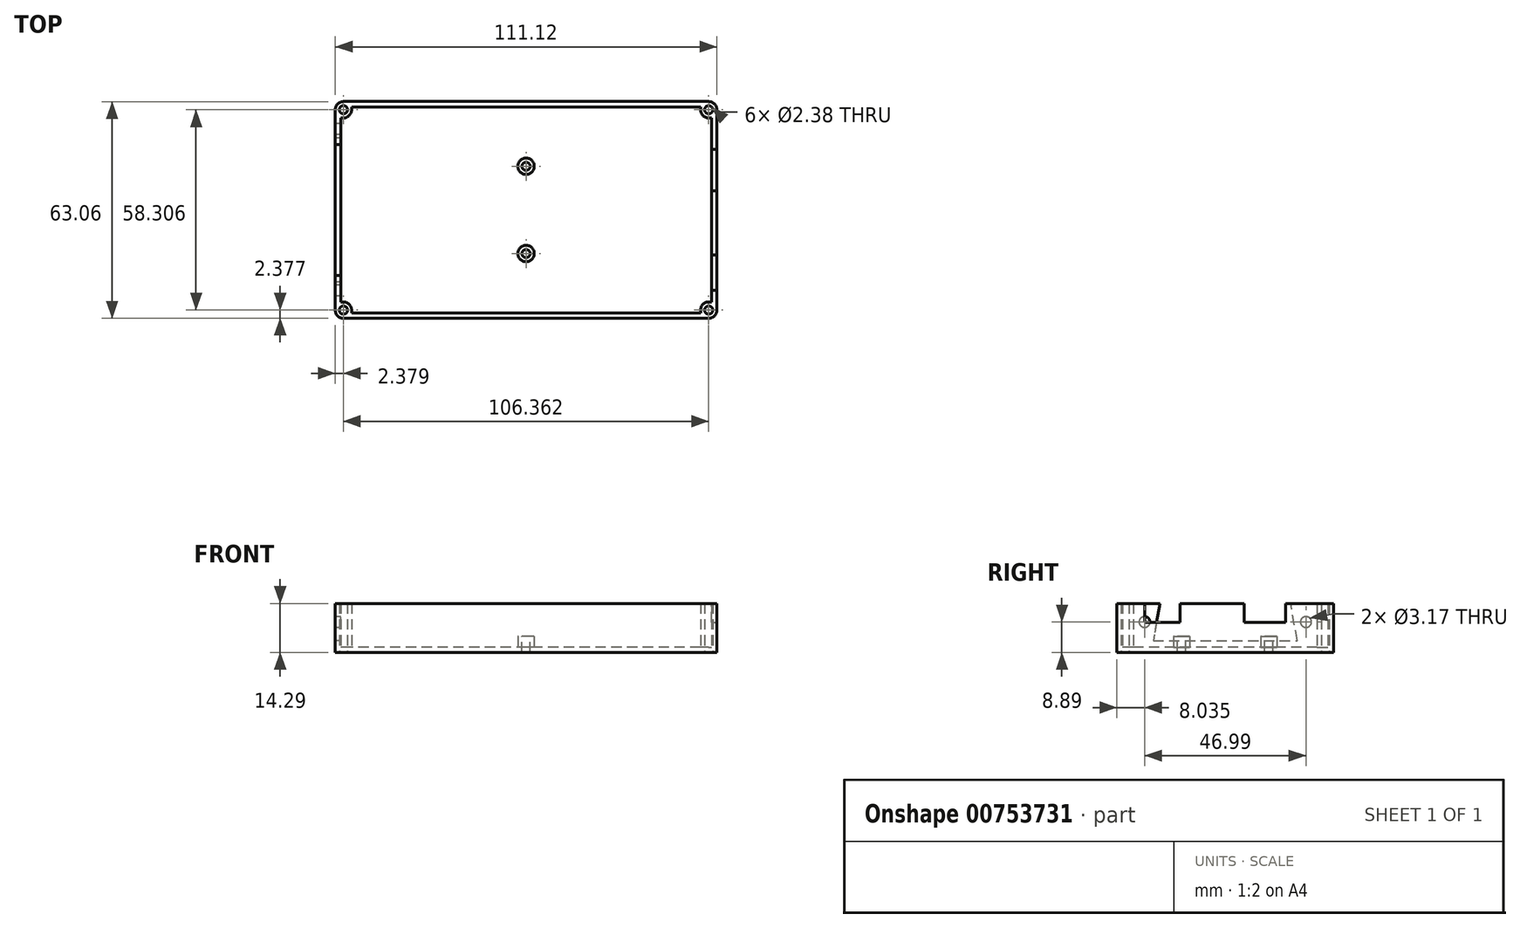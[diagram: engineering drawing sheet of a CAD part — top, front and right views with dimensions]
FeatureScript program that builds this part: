
annotation { "Feature Type Name" : "Feature", "Feature Type Description" : "" }
export const myFeature = defineFeature(function(context is Context, id is Id, definition is map)
    precondition{}
    {
        {
            var Q0;
            Q0=qCreatedBy(makeId("Top.planeOp"),FACE);
            var sketch = newSketch(context, id + "F0", { "sketchPlane" : qUnion([Q0])});
            skLineSegment(sketch, "E0.bottom", {"start": v(50.8, 26.77) * mm, "end": v(-50.8, 26.77) * mm});
            skLineSegment(sketch, "E0.top", {"start": v(50.8, -26.77) * mm, "end": v(-50.8, -26.77) * mm});
            skLineSegment(sketch, "E0.left", {"start": v(50.8, 26.77) * mm, "end": v(50.8, -26.77) * mm});
            skLineSegment(sketch, "E0.right", {"start": v(-50.8, 26.77) * mm, "end": v(-50.8, -26.77) * mm});
            skPoint(sketch, "E0.middle", {"position": v(0, 0) * mm});
            skSolve(sketch);
        }
        {
            var Q0;
            Q0=qCreatedBy(makeId("Top.planeOp"),FACE);
            var sketch = newSketch(context, id + "F1", { "sketchPlane" : qUnion([Q0])});
            skLineSegment(sketch, "E1.bottom", {"start": v(55.56, 31.53) * mm, "end": v(-55.56, 31.53) * mm});
            skLineSegment(sketch, "E1.top", {"start": v(55.56, -31.53) * mm, "end": v(-55.56, -31.53) * mm});
            skLineSegment(sketch, "E1.left", {"start": v(55.56, 31.53) * mm, "end": v(55.56, -31.53) * mm});
            skLineSegment(sketch, "E1.right", {"start": v(-55.56, 31.53) * mm, "end": v(-55.56, -31.53) * mm});
            skPoint(sketch, "E1.middle", {"position": v(0, 0) * mm});
            skLineSegment(sketch, "E2.bottom", {"start": v(53.97, 29.95) * mm, "end": v(-53.98, 29.95) * mm, "construction": true});
            skLineSegment(sketch, "E2.top", {"start": v(53.98, -29.95) * mm, "end": v(-53.97, -29.95) * mm, "construction": true});
            skLineSegment(sketch, "E2.left", {"start": v(53.97, 29.95) * mm, "end": v(53.98, -29.95) * mm, "construction": true});
            skLineSegment(sketch, "E2.right", {"start": v(-53.98, 29.95) * mm, "end": v(-53.97, -29.95) * mm, "construction": true});
            skSolve(sketch);
        }
        {
            var Q0;
            Q0=makeQuery(id+"F1.imprint","IMPRINT",FACE,{"disambiguationData":[TD([[makeQuery(id+"F1.imprint","IMPRINT",EDGE,{"derivedFrom":sQuery(id+"F1.wireOp",EDGE,"E1.bottom")}),1.0]])]});
            extrude(context, id + "F2", {"entities" : qUnion([Q0]), "depth" : 1.59 * mm, "offsetDistance" : 25.4 * mm});
        }
        {
            var Q0;
            Q0=makeQuery(id+"F2.opExtrude","CAP_FACE",FACE,{"disambiguationData":[OSD([sQuery(id+"F1.wireOp",EDGE,"E1.bottom"),sQuery(id+"F1.wireOp",EDGE,"E1.top"),sQuery(id+"F1.wireOp",EDGE,"E1.left"),sQuery(id+"F1.wireOp",EDGE,"E1.right")])],"isStart":false});
            var sketch = newSketch(context, id + "F3", { "sketchPlane" : qUnion([Q0])});
            skLineSegment(sketch, "E3.bottom", {"start": v(55.56, 31.53) * mm, "end": v(-55.56, 31.53) * mm});
            skLineSegment(sketch, "E3.top", {"start": v(55.56, -31.53) * mm, "end": v(-55.56, -31.53) * mm});
            skLineSegment(sketch, "E3.left", {"start": v(55.56, 31.53) * mm, "end": v(55.56, -31.53) * mm});
            skLineSegment(sketch, "E3.right", {"start": v(-55.56, 31.53) * mm, "end": v(-55.56, -31.53) * mm});
            skPoint(sketch, "E3.middle", {"position": v(0, 0) * mm});
            skLineSegment(sketch, "E4.left", {"start": v(53.97, 26.77) * mm, "end": v(53.97, -26.77) * mm});
            skLineSegment(sketch, "E4.right", {"start": v(-53.97, 26.77) * mm, "end": v(-53.97, -26.77) * mm});
            skArc(sketch, "E5", {"start": v(-53.18, 26.77) * mm, "mid": v(-51.5, 27.47) * mm, "end": v(-50.8, 29.15) * mm});
            skCircle(sketch, "E6", {"center": v(-53.18, 29.15) * mm, "radius": 1.2 * mm});
            skLineSegment(sketch, "E7", {"start": v(-50.8, 29.15) * mm, "end": v(-50.8, 29.95) * mm});
            skLineSegment(sketch, "E8", {"start": v(-53.18, 26.77) * mm, "end": v(-53.97, 26.77) * mm});
            skLineSegment(sketch, "E9", {"start": v(-55.56, 31.53) * mm, "end": v(-51.5, 27.47) * mm, "construction": true});
            skPoint(sketch, "E10", {"position": v(-53.53, 29.5) * mm});
            skPoint(sketch, "E11.orphan", {"position": v(-53.97, 37.1) * mm});
            skCircle(sketch, "E12.MirrorC", {"center": v(-53.18, -29.15) * mm, "radius": 1.2 * mm});
            skLineSegment(sketch, "E13.MirrorCS", {"start": v(-53.18, -26.77) * mm, "end": v(-53.97, -26.77) * mm});
            skArc(sketch, "E14.MirrorCS", {"start": v(-53.18, -26.77) * mm, "mid": v(-51.5, -27.47) * mm, "end": v(-50.8, -29.15) * mm});
            skLineSegment(sketch, "E15.MirrorCS", {"start": v(-50.8, -29.15) * mm, "end": v(-50.8, -29.95) * mm});
            skCircle(sketch, "E16.MirrorC", {"center": v(53.18, 29.15) * mm, "radius": 1.2 * mm});
            skLineSegment(sketch, "E17.MirrorCS", {"start": v(50.8, 29.15) * mm, "end": v(50.8, 29.95) * mm});
            skArc(sketch, "E18.MirrorCS", {"start": v(53.18, 26.77) * mm, "mid": v(51.5, 27.47) * mm, "end": v(50.8, 29.15) * mm});
            skLineSegment(sketch, "E19.MirrorCS", {"start": v(53.18, 26.77) * mm, "end": v(53.97, 26.77) * mm});
            skCircle(sketch, "E20.MirrorC", {"center": v(53.18, -29.15) * mm, "radius": 1.2 * mm});
            skLineSegment(sketch, "E21.MirrorCS", {"start": v(53.18, -26.77) * mm, "end": v(53.97, -26.77) * mm});
            skArc(sketch, "E22.MirrorCS", {"start": v(53.18, -26.77) * mm, "mid": v(51.5, -27.47) * mm, "end": v(50.8, -29.15) * mm});
            skLineSegment(sketch, "E23.MirrorCS", {"start": v(50.8, -29.15) * mm, "end": v(50.8, -29.95) * mm});
            skPoint(sketch, "E24.orphan", {"position": v(-53.97, -36.92) * mm});
            skLineSegment(sketch, "E25.trimOffspring", {"start": v(50.8, -29.95) * mm, "end": v(-50.8, -29.95) * mm});
            skPoint(sketch, "E26.orphan", {"position": v(53.97, -37.1) * mm});
            skLineSegment(sketch, "E27.trimOffspring", {"start": v(50.8, 29.95) * mm, "end": v(-50.8, 29.95) * mm});
            skPoint(sketch, "E28.orphan", {"position": v(53.97, 36.92) * mm});
            skSolve(sketch);
        }
        {
            var Q0;
            Q0=qSketchRegion(id+"F3",true);
            extrude(context, id + "F4", {"entities" : qUnion([Q0]), "operationType" : NewBodyOperationType.ADD, "depth" : 12.7 * mm, "offsetDistance" : 25.4 * mm});
        }
        {
            var Q0;
            Q0=makeQuery(id+"F4.boolean.opBoolean","MERGE",EDGE,{"derivedFrom":[makeQuery(id+"F2.opExtrude","SWEPT_EDGE",EDGE,{"disambiguationData":[OSD([sQuery(id+"F1.wireOp",EDGE,"E1.top"),sQuery(id+"F1.wireOp",EDGE,"E1.left")])]}),makeQuery(id+"F4.opExtrude","SWEPT_EDGE",EDGE,{"disambiguationData":[OSD([sQuery(id+"F3.wireOp",EDGE,"E3.top"),sQuery(id+"F3.wireOp",EDGE,"E3.left")])]})]});
            var Q1;
            Q1=makeQuery(id+"F4.boolean.opBoolean","MERGE",EDGE,{"derivedFrom":[makeQuery(id+"F2.opExtrude","SWEPT_EDGE",EDGE,{"disambiguationData":[OSD([sQuery(id+"F1.wireOp",EDGE,"E1.bottom"),sQuery(id+"F1.wireOp",EDGE,"E1.left")])]}),makeQuery(id+"F4.opExtrude","SWEPT_EDGE",EDGE,{"disambiguationData":[OSD([sQuery(id+"F3.wireOp",EDGE,"E3.bottom"),sQuery(id+"F3.wireOp",EDGE,"E3.left")])]})]});
            var Q2;
            Q2=makeQuery(id+"F4.boolean.opBoolean","MERGE",EDGE,{"derivedFrom":[makeQuery(id+"F2.opExtrude","SWEPT_EDGE",EDGE,{"disambiguationData":[OSD([sQuery(id+"F1.wireOp",EDGE,"E1.top"),sQuery(id+"F1.wireOp",EDGE,"E1.right")])]}),makeQuery(id+"F4.opExtrude","SWEPT_EDGE",EDGE,{"disambiguationData":[OSD([sQuery(id+"F3.wireOp",EDGE,"E3.top"),sQuery(id+"F3.wireOp",EDGE,"E3.right")])]})]});
            var Q3;
            Q3=makeQuery(id+"F4.boolean.opBoolean","MERGE",EDGE,{"derivedFrom":[makeQuery(id+"F2.opExtrude","SWEPT_EDGE",EDGE,{"disambiguationData":[OSD([sQuery(id+"F1.wireOp",EDGE,"E1.bottom"),sQuery(id+"F1.wireOp",EDGE,"E1.right")])]}),makeQuery(id+"F4.opExtrude","SWEPT_EDGE",EDGE,{"disambiguationData":[OSD([sQuery(id+"F3.wireOp",EDGE,"E3.bottom"),sQuery(id+"F3.wireOp",EDGE,"E3.right")])]})]});
            fillet(context, id + "F5", {"entities" : qUnion([Q0, Q1, Q2, Q3]), "radius" : 2.38 * mm, "tangentPropagation" : true, "allowEdgeOverflow" : false});
        }
        {
            var Q0;
            Q0=makeQuery(id+"F4.boolean.opBoolean","MERGE",FACE,{"derivedFrom":[makeQuery(id+"F2.opExtrude","SWEPT_FACE",FACE,{"disambiguationData":[OSD([sQuery(id+"F1.wireOp",EDGE,"E1.left")])]}),makeQuery(id+"F4.opExtrude","SWEPT_FACE",FACE,{"disambiguationData":[OSD([sQuery(id+"F3.wireOp",EDGE,"E3.left")])]})]});
            var sketch = newSketch(context, id + "F6", { "sketchPlane" : qUnion([Q0])});
            skLineSegment(sketch, "E29.bottom", {"start": v(-17.59, 14.29) * mm, "end": v(-13.14, 14.29) * mm});
            skLineSegment(sketch, "E29.top", {"start": v(-17.59, 8.76) * mm, "end": v(-13.14, 8.76) * mm});
            skLineSegment(sketch, "E30.top", {"start": v(13.14, 8.76) * mm, "end": v(17.59, 8.76) * mm});
            skPoint(sketch, "E31", {"position": v(-11.56, 8.76) * mm});
            skPoint(sketch, "E32", {"position": v(18.29, 8.76) * mm});
            skLineSegment(sketch, "E33.MirrorCS", {"start": v(5.52, 14.29) * mm, "end": v(5.52, 8.76) * mm});
            skLineSegment(sketch, "E34.MirrorCS", {"start": v(13.14, 8.76) * mm, "end": v(5.52, 8.76) * mm});
            skLineSegment(sketch, "E35.MirrorCS", {"start": v(17.59, 14.29) * mm, "end": v(17.59, 8.76) * mm});
            skLineSegment(sketch, "E36.MirrorCS", {"start": v(-17.59, 14.29) * mm, "end": v(-23.43, 14.29) * mm});
            skLineSegment(sketch, "E37.MirrorCS", {"start": v(-17.59, 8.76) * mm, "end": v(-23.43, 8.76) * mm});
            skPoint(sketch, "E38.MirrorP", {"position": v(-18.29, 8.76) * mm});
            skLineSegment(sketch, "E39.MirrorCS", {"start": v(-13.14, 14.29) * mm, "end": v(-13.14, 8.76) * mm});
            skLineSegment(sketch, "E40.MirrorCS", {"start": v(-23.43, 14.29) * mm, "end": v(-23.43, 8.76) * mm});
            skLineSegment(sketch, "E41.MirrorCS", {"start": v(17.59, 14.29) * mm, "end": v(5.52, 14.29) * mm});
            skPoint(sketch, "E42.MirrorP", {"position": v(11.56, 8.76) * mm});
            skPoint(sketch, "E43.orphan", {"position": v(23.43, 14.29) * mm});
            skPoint(sketch, "E44.orphan", {"position": v(23.43, 8.76) * mm});
            skPoint(sketch, "E30.bottom.start.orphan", {"position": v(13.14, 14.29) * mm});
            skPoint(sketch, "E29.right.end.orphan", {"position": v(-5.52, 8.76) * mm});
            skPoint(sketch, "E45.orphan", {"position": v(-5.52, 14.29) * mm});
            skSolve(sketch);
        }
        {
            var Q0;
            Q0=qSketchRegion(id+"F6",true);
            extrude(context, id + "F7", {"entities" : qUnion([Q0]), "operationType" : NewBodyOperationType.REMOVE, "endBound" : BoundingType.UP_TO_NEXT, "oppositeDirection" : true, "depth" : 25.4 * mm, "offsetDistance" : 25.4 * mm});
        }
        {
            var Q0;
            Q0=makeQuery(id+"F0.imprint","IMPRINT",FACE,{"disambiguationData":[TD([[makeQuery(id+"F0.imprint","IMPRINT",EDGE,{"derivedFrom":sQuery(id+"F0.wireOp",EDGE,"E0.bottom")}),1.0]])]});
            var sketch = newSketch(context, id + "F8", { "sketchPlane" : qUnion([Q0])});
            skLineSegment(sketch, "E46.bottom", {"start": v(-42.55, -25.36) * mm, "end": v(33.02, -25.36) * mm});
            skLineSegment(sketch, "E46.top", {"start": v(-42.55, -22.18) * mm, "end": v(33.02, -22.18) * mm});
            skLineSegment(sketch, "E46.left", {"start": v(-42.55, -25.36) * mm, "end": v(-42.55, -22.18) * mm});
            skLineSegment(sketch, "E46.right", {"start": v(33.02, -25.36) * mm, "end": v(33.02, -22.18) * mm});
            skPoint(sketch, "E47", {"position": v(-42.55, -23.77) * mm});
            skLineSegment(sketch, "E48.MirrorCS", {"start": v(33.02, 25.36) * mm, "end": v(33.02, 22.18) * mm});
            skLineSegment(sketch, "E49.MirrorCS", {"start": v(-42.55, 25.36) * mm, "end": v(-42.55, 22.18) * mm});
            skLineSegment(sketch, "E50.MirrorCS", {"start": v(-42.55, 22.18) * mm, "end": v(33.02, 22.18) * mm});
            skLineSegment(sketch, "E51.MirrorCS", {"start": v(-42.55, 25.36) * mm, "end": v(33.02, 25.36) * mm});
            skPoint(sketch, "E52.MirrorP", {"position": v(-42.55, 23.77) * mm});
            skSolve(sketch);
        }
        {
            var Q0;
            Q0=makeQuery(id+"F4.boolean.opBoolean","MERGE",FACE,{"derivedFrom":[makeQuery(id+"F2.opExtrude","SWEPT_FACE",FACE,{"disambiguationData":[OSD([sQuery(id+"F1.wireOp",EDGE,"E1.right")])]}),makeQuery(id+"F4.opExtrude","SWEPT_FACE",FACE,{"disambiguationData":[OSD([sQuery(id+"F3.wireOp",EDGE,"E3.right")])]})]});
            var sketch = newSketch(context, id + "F9", { "sketchPlane" : qUnion([Q0])});
            skLineSegment(sketch, "E53", {"start": v(-19.05, 14.29) * mm, "end": v(19.05, 14.29) * mm});
            skLineSegment(sketch, "E54", {"start": v(19.05, 14.29) * mm, "end": v(20.95, 3.5) * mm});
            skLineSegment(sketch, "E55", {"start": v(20.95, 3.5) * mm, "end": v(-20.96, 3.5) * mm});
            skLineSegment(sketch, "E56", {"start": v(-20.96, 3.5) * mm, "end": v(-19.05, 14.29) * mm});
            skPoint(sketch, "E57", {"position": v(0, 14.29) * mm});
            skPoint(sketch, "E58", {"position": v(0, 3.5) * mm});
            skCircle(sketch, "E59", {"center": v(-23.5, 8.9) * mm, "radius": 1.59 * mm});
            skCircle(sketch, "E60", {"center": v(23.5, 8.9) * mm, "radius": 1.59 * mm});
            skLineSegment(sketch, "E61", {"start": v(0, 14.29) * mm, "end": v(0, 3.5) * mm, "construction": true});
            skPoint(sketch, "E62", {"position": v(0, 8.89) * mm});
            skSolve(sketch);
        }
        {
            var Q0;
            Q0=qSketchRegion(id+"F9",true);
            extrude(context, id + "F10", {"entities" : qUnion([Q0]), "operationType" : NewBodyOperationType.REMOVE, "endBound" : BoundingType.UP_TO_NEXT, "oppositeDirection" : true, "depth" : 25.4 * mm, "offsetDistance" : 25.4 * mm});
        }
        {
            var Q0;
            Q0=makeQuery(id+"F4.boolean.opBoolean","SPLIT",FACE,{"disambiguationData":[TD([makeQuery(id+"F4.opExtrude","SWEPT_FACE",FACE,{"disambiguationData":[OSD([sQuery(id+"F3.wireOp",EDGE,"E4.left")])]})])],"derivedFrom":makeQuery(id+"F2.opExtrude","CAP_FACE",FACE,{"disambiguationData":[OSD([sQuery(id+"F1.wireOp",EDGE,"E1.bottom"),sQuery(id+"F1.wireOp",EDGE,"E1.top"),sQuery(id+"F1.wireOp",EDGE,"E1.left"),sQuery(id+"F1.wireOp",EDGE,"E1.right")])],"isStart":false})});
            var sketch = newSketch(context, id + "F11", { "sketchPlane" : qUnion([Q0])});
            skCircle(sketch, "E63", {"center": v(0, 12.7) * mm, "radius": 2.38 * mm});
            skCircle(sketch, "E64.MirrorC", {"center": v(0, -12.7) * mm, "radius": 2.38 * mm});
            skSolve(sketch);
        }
        {
            var Q0;
            Q0=qSketchRegion(id+"F11",true);
            extrude(context, id + "F12", {"entities" : qUnion([Q0]), "operationType" : NewBodyOperationType.ADD, "depth" : 3.17 * mm, "offsetDistance" : 25.4 * mm});
        }
        {
            var Q0;
            Q0=makeQuery(id+"F12.opExtrude","CAP_FACE",FACE,{"disambiguationData":[OSD([sQuery(id+"F11.wireOp",EDGE,"E63")])],"isStart":false});
            var sketch = newSketch(context, id + "F13", { "sketchPlane" : qUnion([Q0])});
            skCircle(sketch, "E65", {"center": v(0, 12.7) * mm, "radius": 1.2 * mm});
            skCircle(sketch, "E66.MirrorC", {"center": v(0, -12.7) * mm, "radius": 1.2 * mm});
            skSolve(sketch);
        }
        {
            var Q0;
            Q0=qSketchRegion(id+"F13",true);
            extrude(context, id + "F14", {"entities" : qUnion([Q0]), "operationType" : NewBodyOperationType.REMOVE, "endBound" : BoundingType.THROUGH_ALL, "oppositeDirection" : true, "depth" : 25.4 * mm, "offsetDistance" : 25.4 * mm});
        }
        {
            var Q0;
            {var subQ0=sQuery(id+"F3.wireOp",EDGE,"E6");var subQ2=sQuery(id+"F3.wireOp",EDGE,"E5");var subQ4=sQuery(id+"F3.wireOp",EDGE,"E4.right");var subQ6=sQuery(id+"F3.wireOp",EDGE,"E4.left");var subQ8=sQuery(id+"F3.wireOp",EDGE,"E3.right");var subQ10=sQuery(id+"F1.wireOp",EDGE,"E1.bottom");var subQ11=makeQuery(id+"F2.opExtrude","SWEPT_FACE",FACE,{"disambiguationData":[OSD([subQ10])]});var subQ12=sQuery(id+"F3.wireOp",EDGE,"E19.MirrorCS");var subQ14=sQuery(id+"F3.wireOp",EDGE,"E3.bottom");var subQ17=sQuery(id+"F3.wireOp",EDGE,"E3.left");var subQ23=sQuery(id+"F3.wireOp",EDGE,"E7");var subQ25=sQuery(id+"F3.wireOp",EDGE,"E8");var subQ28=sQuery(id+"F3.wireOp",EDGE,"E16.MirrorC");var subQ30=sQuery(id+"F3.wireOp",EDGE,"E17.MirrorCS");var subQ32=sQuery(id+"F3.wireOp",EDGE,"E18.MirrorCS");var subQ35=sQuery(id+"F3.wireOp",EDGE,"E27.trimOffspring");var subQ37=sQuery(id+"F3.wireOp",EDGE,"E15.MirrorCS");var subQ38=sQuery(id+"F3.wireOp",EDGE,"E14.MirrorCS");var subQ39=sQuery(id+"F3.wireOp",EDGE,"E13.MirrorCS");var subQ40=sQuery(id+"F3.wireOp",EDGE,"E12.MirrorC");var subQ41=sQuery(id+"F3.wireOp",EDGE,"E3.top");var subQ43=sQuery(id+"F3.wireOp",EDGE,"E22.MirrorCS");var subQ44=sQuery(id+"F3.wireOp",EDGE,"E25.trimOffspring");var subQ45=sQuery(id+"F3.wireOp",EDGE,"E23.MirrorCS");var subQ46=sQuery(id+"F3.wireOp",EDGE,"E20.MirrorC");var subQ47=sQuery(id+"F3.wireOp",EDGE,"E21.MirrorCS");Q0=makeQuery(id+"F10.boolean.opBoolean","SPLIT",FACE,{"disambiguationData":[TD([subQ11])],"derivedFrom":makeQuery(id+"F7.boolean.opBoolean","SPLIT",FACE,{"disambiguationData":[TD([subQ11])],"derivedFrom":makeQuery(id+"F4.opExtrude","CAP_FACE",FACE,{"disambiguationData":[OSD([subQ14,subQ41,subQ17,subQ8,subQ6,subQ4,subQ2,subQ0,subQ23,subQ25,subQ40,subQ39,subQ38,subQ37,subQ28,subQ30,subQ32,subQ12,subQ46,subQ47,subQ43,subQ45,subQ44,subQ35])],"isStart":false})})});}
            var sketch = newSketch(context, id + "F15", { "sketchPlane" : qUnion([Q0])});
            skCircle(sketch, "E67.0", {"center": v(53.18, 29.15) * mm, "radius": 1.2 * mm});
            skCircle(sketch, "E68.0", {"center": v(53.18, -29.15) * mm, "radius": 1.2 * mm});
            skCircle(sketch, "E69.0", {"center": v(-53.18, -29.15) * mm, "radius": 1.2 * mm});
            skCircle(sketch, "E70.0", {"center": v(-53.18, 29.15) * mm, "radius": 1.2 * mm});
            skSolve(sketch);
        }
        {
            var Q0;
            Q0=qSketchRegion(id+"F15",true);
            extrude(context, id + "F16", {"entities" : qUnion([Q0]), "operationType" : NewBodyOperationType.REMOVE, "endBound" : BoundingType.THROUGH_ALL, "oppositeDirection" : true, "depth" : 25.4 * mm, "offsetDistance" : 25.4 * mm});
        }
    });
